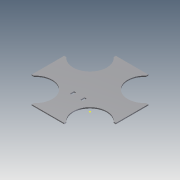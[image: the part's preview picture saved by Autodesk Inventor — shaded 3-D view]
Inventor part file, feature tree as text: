
AUTODESK INVENTOR PART (.ipt)
format: ipt  version: 2011 (Build 150239000, 239)  size: 738,816 bytes
history: native  units: in
note: dims shown in document units (in); Inventor stores cm internally (conversion verified against a paired STEP export)
features: sketch x22, extrude x21, fillet x4
ambient origin geometry x8: Origin, YZ Plane, XZ Plane, XY Plane, X Axis, Y Axis, Z Axis, Center Point
bodies: Solid1 (feature_tree)
feature tree (47):
  sketch  "Sketch1"  dims[d0=20.0in d1=20.0in d2=3.5in]
  extrude  "Extrusion1"  Depth=20.0in
  fillet  "Fillet1"  Radius=3.5in
  extrude  "Extrusion2"  Depth=3.5in
  extrude  "Extrusion3"  Depth=3.5in
  extrude  "Extrusion4"  Depth=3.5in
  extrude  "Extrusion5"  Depth=7.5in
  extrude  "Extrusion6"  Depth=7.5in
  extrude  "Extrusion7"  Depth=7.5in
  extrude  "Extrusion8"  Depth=0.5in TaperAngle=0.0deg
  extrude  "Extrusion9"  Depth=0.5in TaperAngle=0.0deg
  extrude  "Extrusion10"  Depth=4.5635in
  extrude  "Extrusion11"  Depth=2.6in
  fillet  "Fillet2"  Radius=2.6in
  fillet  "Fillet3"  Radius=5.2in
  fillet  "Fillet4"  Radius=5.2in
  extrude  "Extrusion12"  Depth=0.25in
  extrude  "Extrusion13"  Depth=0.25in
  extrude  "Extrusion14"  Depth=0.25in
  extrude  "Extrusion15"  Depth=0.25in
  extrude  "Extrusion16"  Depth=0.25in
  extrude  "Extrusion17"  Depth=0.25in
  extrude  "Extrusion18"  Depth=1.0in TaperAngle=0.0deg
  extrude  "Extrusion19"  Depth=1.5in
  extrude  "Extrusion20"  Depth=1.5in
  extrude  "Extrusion21"  Depth=0.25in
  sketch  "Sketch2"  dims[d3=3.5in d4=3.5in]
  sketch  "Sketch3"  dims[d5=3.5in d6=3.5in]
  sketch  "Sketch4"  dims[d7=3.5in d8=3.5in]
  sketch  "Sketch5"  dims[d9=3.5in d10=7.5in]
  sketch  "Sketch6"  dims[d11=7.5in d12=7.5in]
  sketch  "Sketch7"  dims[d13=7.5in d14=7.5in]
  sketch  "Sketch8"  dims[d15=7.5in d16=0.5in d17=0.0in]
  sketch  "Sketch9"  dims[d18=4.0in d19=0.5in d20=0.0in]
  sketch  "Sketch10"  dims[d21=0.5in d22=0.0in d23=4.5635in]
  sketch  "Sketch11"  dims[d24=4.5635in d25=2.6in d26=2.6in d27=5.2in d28=5.2in]
  sketch  "Sketch12"  dims[d29=0.25in d30=0.25in]
  sketch  "Sketch13"  dims[d31=0.25in d32=0.25in]
  sketch  "Sketch14"  dims[d33=0.25in d34=0.25in]
  sketch  "Sketch15"  dims[d35=5.2in d36=0.25in]
  sketch  "Sketch16"  dims[d37=0.25in d38=0.25in]
  sketch  "Sketch17"  dims[d39=0.25in d40=0.25in]
  sketch  "Sketch18"  dims[d41=0.25in d42=1.0in d43=0.0in]
  sketch  "Sketch19"  dims[d44=0.25in d45=0.0in d46=1.5in]
  sketch  "Sketch20"  dims[d47=1.5in d48=1.5in]
  sketch  "Sketch21"  dims[d49=1.5in d50=0.25in]
  sketch  "Sketch22"  dims[d51=0.25in d52=0.25in d53=0.25in d54=0.25in d55=0.25in d56=0.25in d57=0.25in d58=0.25in d59=0.25in d60=0.25in d61=0.25in d62=0.25in d63=0.0in d64=1.5in d65=1.5in d66=0.25in d67=0.5in d68=1.0in d69=0.25in d70=1.0in d71=1.0in d72=1.0in d73=0.5in d74=0.5in d75=1.0in d76=0.0in d77=0.25in d78=0.0in d79=4.5635in d80=0.6in d81=1.2in d82=0.5in d83=0.25in d84=0.5in d85=0.25in d86=1.0in d87=1.0in d88=1.0in d89=1.0in d90=0.25in d91=0.0in d92=0.25in d93=0.0in d94=1.0in d95=1.0in d96=0.25in d97=0.0in d98=0.125in d99=0.125in d100=0.125in d101=0.25in d102=0.25in d103=0.25in d104=0.25in d105=0.25in d106=0.25in d107=0.25in d108=0.25in d109=0.0in d110=0.25in d111=0.25in d112=0.25in d113=0.0in d114=0.25in d115=0.0in d116=2.85in d117=5.7in d118=0.75in d119=0.5in d120=0.75in d121=0.25in d122=0.0in d123=0.25in d124=0.0in d125=0.5in d126=0.25in d127=0.0in d128=0.5in d129=0.25in d130=0.0in d131=3.85in d132=7.7in d133=0.25in d134=0.0in d135=3.85in d136=7.7in d137=1.0in d138=0.0in d139=9.0in d140=7.7in d141=9.0in d142=0.5in d143=1.0in d144=0.5in d145=1.0in d146=1.0in d147=0.0in]
